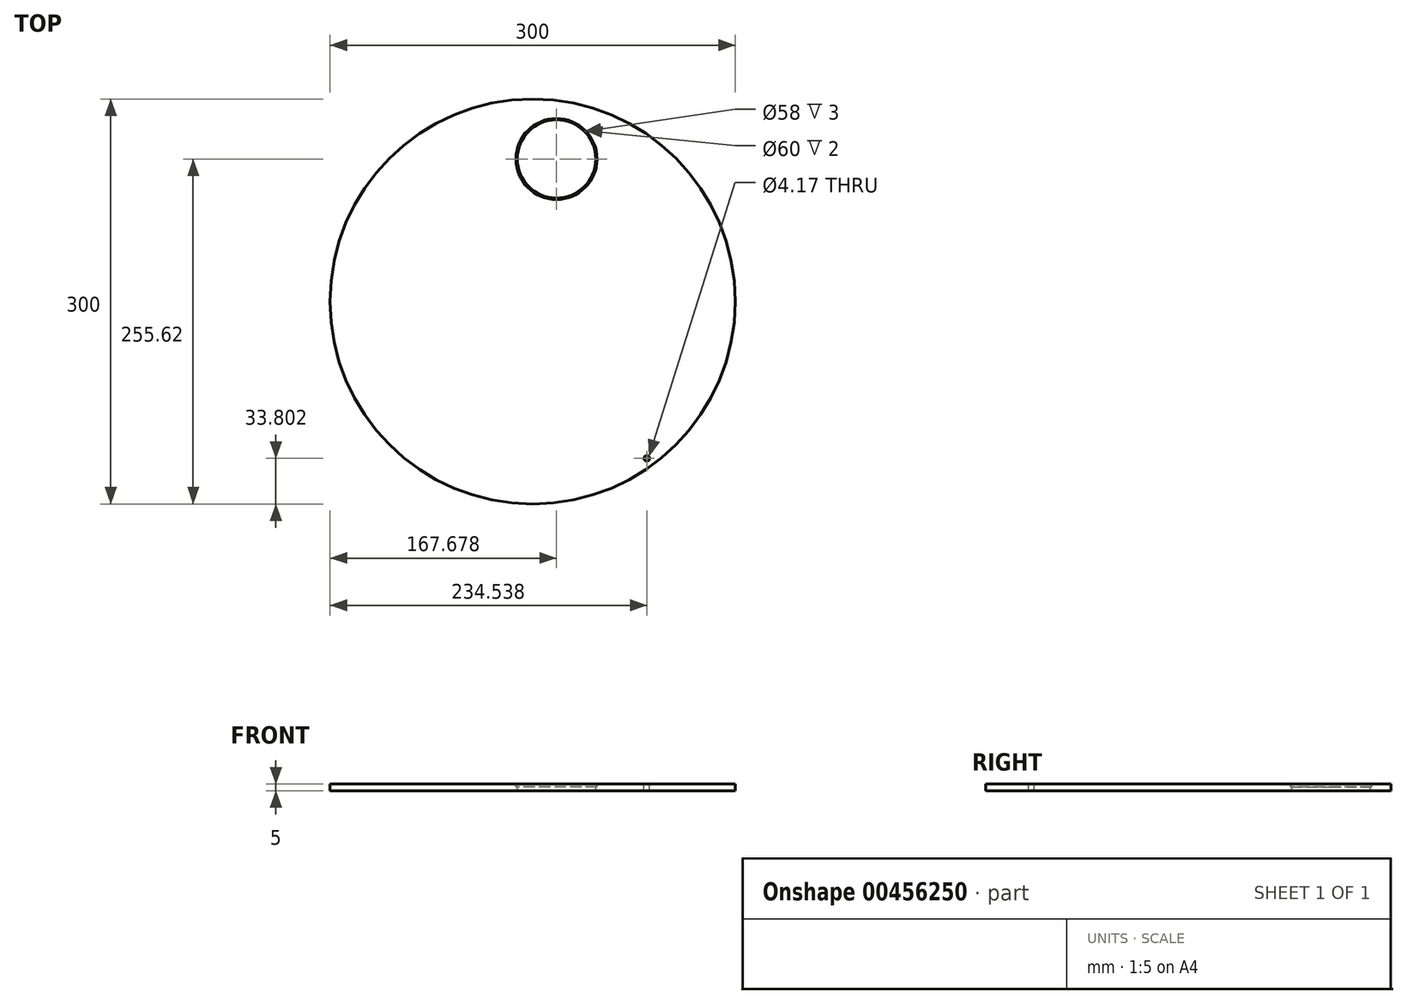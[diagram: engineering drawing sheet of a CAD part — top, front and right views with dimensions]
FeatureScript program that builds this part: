
annotation { "Feature Type Name" : "Feature", "Feature Type Description" : "" }
export const myFeature = defineFeature(function(context is Context, id is Id, definition is map)
    precondition{}
    {
        {
            var Q0;
            Q0=qCreatedBy(makeId("Top.planeOp"),FACE);
            var sketch = newSketch(context, id + "F0", { "sketchPlane" : qUnion([Q0])});
            skCircle(sketch, "E0", {"center": v(0, 0) * mm, "radius": 150 * mm});
            skSolve(sketch);
        }
        {
            var Q0;
            Q0=makeQuery(id+"F0.imprint","IMPRINT",FACE,{"disambiguationData":[TD([[makeQuery(id+"F0.imprint","IMPRINT",EDGE,{"derivedFrom":sQuery(id+"F0.wireOp",EDGE,"E0")}),1.0]])]});
            extrude(context, id + "F1", {"entities" : qUnion([Q0]), "endBound" : BoundingType.SYMMETRIC, "depth" : 5 * mm});
        }
        {
            var Q0;
            Q0=makeQuery(id+"F1.opExtrude","CAP_FACE",FACE,{"disambiguationData":[OSD([sQuery(id+"F0.wireOp",EDGE,"E0")])],"isStart":false});
            var sketch = newSketch(context, id + "F2", { "sketchPlane" : qUnion([Q0])});
            skCircle(sketch, "E1", {"center": v(17.68, 105.62) * mm, "radius": 30 * mm});
            skCircle(sketch, "E2", {"center": v(0, 0) * mm, "radius": 107.5 * mm, "construction": true});
            skCircle(sketch, "E3", {"center": v(17.68, 105.62) * mm, "radius": 29 * mm});
            skSolve(sketch);
        }
        {
            var Q0;
            Q0=makeQuery(id+"F2.imprint","IMPRINT",FACE,{"disambiguationData":[TD([[makeQuery(id+"F2.imprint","IMPRINT",EDGE,{"derivedFrom":sQuery(id+"F2.wireOp",EDGE,"E3")}),1.0]])]});
            extrude(context, id + "F3", {"entities" : qUnion([Q0]), "operationType" : NewBodyOperationType.REMOVE, "endBound" : BoundingType.THROUGH_ALL, "oppositeDirection" : true, "depth" : 25 * mm});
        }
        {
            var Q0;
            Q0=makeQuery(id+"F2.imprint","IMPRINT",FACE,{"disambiguationData":[TD([[makeQuery(id+"F2.imprint","IMPRINT",EDGE,{"derivedFrom":sQuery(id+"F2.wireOp",EDGE,"E1")}),1.0]])]});
            extrude(context, id + "F4", {"entities" : qUnion([Q0]), "operationType" : NewBodyOperationType.REMOVE, "oppositeDirection" : true, "depth" : 2 * mm});
        }
        {
            var Q0;
            Q0=makeQuery(id+"F2.imprint","IMPRINT",FACE,{"disambiguationData":[TD([[makeQuery(id+"F2.imprint","IMPRINT",EDGE,{"derivedFrom":sQuery(id+"F2.wireOp",EDGE,"E1")}),-1.0]])]});
            var sketch = newSketch(context, id + "F5", { "sketchPlane" : qUnion([Q0])});
            skCircle(sketch, "E4", {"center": v(84.54, -116.2) * mm, "radius": 2.09 * mm});
            skSolve(sketch);
        }
        {
            var Q0;
            Q0 = qSketchRegion(id + "F5", true);
            extrude(context, id + "F6", {"entities" : qUnion([Q0]), "operationType" : NewBodyOperationType.REMOVE, "endBound" : BoundingType.THROUGH_ALL, "oppositeDirection" : true, "depth" : 25 * mm});
        }
    });
